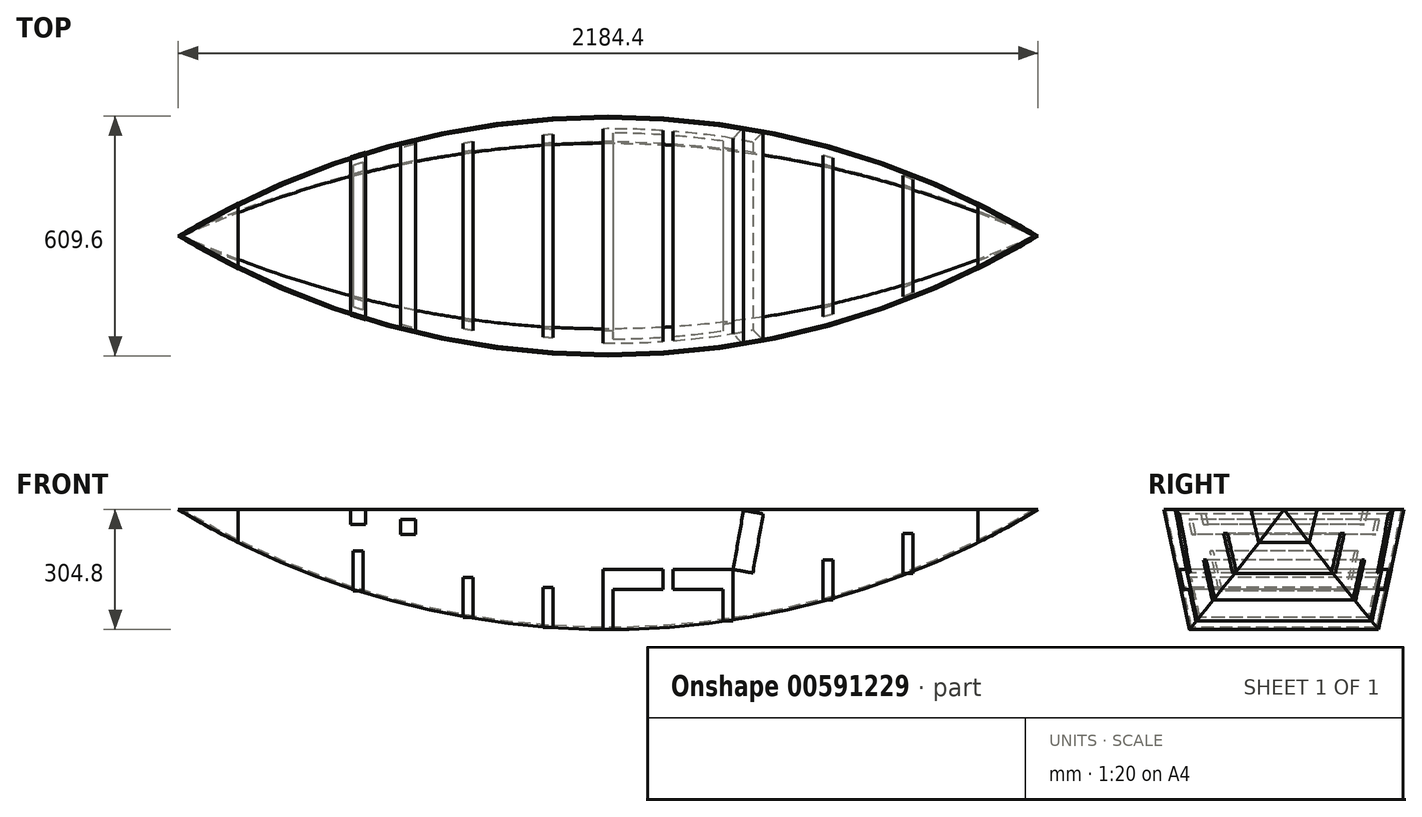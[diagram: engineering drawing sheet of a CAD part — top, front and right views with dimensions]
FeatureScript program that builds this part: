
annotation { "Feature Type Name" : "Feature", "Feature Type Description" : "" }
export const myFeature = defineFeature(function(context is Context, id is Id, definition is map)
    precondition{}
    {
        {
            var Q0;
            Q0=qCreatedBy(makeId("Front.planeOp"),FACE);
            var sketch = newSketch(context, id + "F0", { "sketchPlane" : qUnion([Q0])});
            skLineSegment(sketch, "E0", {"start": v(0, 0) * mm, "end": v(2184.4, 0) * mm});
            skArc(sketch, "E1", {"start": v(0, 0) * mm, "mid": v(1092.2, -304.8) * mm, "end": v(2184.4, 0) * mm});
            skSolve(sketch);
        }
        {
            var Q0;
            Q0 = qSketchRegion(id + "F0", true);
            extrude(context, id + "F1", {"entities" : qUnion([Q0]), "oppositeDirection" : true, "depth" : 609.6 * mm, "offsetDistance" : 25.4 * mm});
        }
        {
            var Q0;
            Q0=makeQuery(id+"F1.opExtrude","SWEPT_FACE",FACE,{"disambiguationData":[OSD([sQuery(id+"F0.wireOp",EDGE,"E0")])]});
            var sketch = newSketch(context, id + "F2", { "sketchPlane" : qUnion([Q0])});
            skLineSegment(sketch, "E2", {"start": v(0, 304.8) * mm, "end": v(2184.4, 304.8) * mm});
            skArc(sketch, "E3", {"start": v(0, 304.8) * mm, "mid": v(1092.2, 0) * mm, "end": v(2184.4, 304.8) * mm});
            skArc(sketch, "E4", {"start": v(2184.4, 304.8) * mm, "mid": v(1092.2, 609.6) * mm, "end": v(0, 304.8) * mm});
            skLineSegment(sketch, "E5.bottom", {"start": v(-93.83, 720.8) * mm, "end": v(2286.33, 720.8) * mm});
            skLineSegment(sketch, "E5.top", {"start": v(-93.83, -163.14) * mm, "end": v(2286.33, -163.14) * mm});
            skLineSegment(sketch, "E5.left", {"start": v(-93.83, 720.8) * mm, "end": v(-93.83, -163.14) * mm});
            skLineSegment(sketch, "E5.right", {"start": v(2286.33, 720.8) * mm, "end": v(2286.33, -163.14) * mm});
            skSolve(sketch);
        }
        {
            var Q0;
            Q0 = qSketchRegion(id + "F2", true);
            extrude(context, id + "F3", {"entities" : qUnion([Q0]), "operationType" : NewBodyOperationType.REMOVE, "oppositeDirection" : true, "depth" : 508 * mm, "offsetDistance" : 25.4 * mm, "hasDraft" : true, "draftAngle" : 12 * degree});
        }
        {
            var Q0;
            Q0=makeQuery(id+"F1.opExtrude","SWEPT_FACE",FACE,{"disambiguationData":[OSD([sQuery(id+"F0.wireOp",EDGE,"E0")])]});
            shell(context, id + "F4", {"entities" : qUnion([Q0]), "thickness" : 5.16 * mm});
        }
        {
            var Q0;
            Q0=qCreatedBy(makeId("Front.planeOp"),FACE);
            var sketch = newSketch(context, id + "F5", { "sketchPlane" : qUnion([Q0])});
            skLineSegment(sketch, "E6.bottom", {"start": v(1079.5, -304.8) * mm, "end": v(1104.9, -304.8) * mm});
            skLineSegment(sketch, "E6.top", {"start": v(1079.5, -203.2) * mm, "end": v(1104.9, -203.2) * mm});
            skLineSegment(sketch, "E6.left", {"start": v(1079.5, -304.8) * mm, "end": v(1079.5, -203.2) * mm});
            skLineSegment(sketch, "E6.right", {"start": v(1104.9, -304.8) * mm, "end": v(1104.9, -203.2) * mm});
            skPoint(sketch, "E7", {"position": v(1092.2, -304.8) * mm});
            skPoint(sketch, "E8", {"position": v(1092.2, 0) * mm});
            skPoint(sketch, "E8.positionSnap0", {"position": v(1092.2, -203.2) * mm});
            skPoint(sketch, "E9", {"position": v(939.8, 0) * mm});
            skPoint(sketch, "E10", {"position": v(457.2, 0) * mm});
            skPoint(sketch, "E11", {"position": v(1397, 0) * mm});
            skPoint(sketch, "E12", {"position": v(1651, 0) * mm});
            skPoint(sketch, "E13", {"position": v(1854.2, 0) * mm});
            skArc(sketch, "E14.0", {"start": v(0, 0) * mm, "mid": v(1092.2, -304.8) * mm, "end": v(2184.4, 0) * mm});
            skPoint(sketch, "E15", {"position": v(939.8, -299.29) * mm});
            skPoint(sketch, "E16", {"position": v(457.2, -206.95) * mm});
            skPoint(sketch, "E17", {"position": v(1397, -282.66) * mm});
            skPoint(sketch, "E18", {"position": v(1651, -229.43) * mm});
            skPoint(sketch, "E19", {"position": v(1854.2, -162.35) * mm});
            skLineSegment(sketch, "E20.bottom", {"start": v(927.1, -197.69) * mm, "end": v(952.5, -197.69) * mm});
            skLineSegment(sketch, "E20.top", {"start": v(927.1, -299.29) * mm, "end": v(952.5, -299.29) * mm});
            skLineSegment(sketch, "E20.left", {"start": v(927.1, -197.69) * mm, "end": v(927.1, -299.29) * mm});
            skLineSegment(sketch, "E20.right", {"start": v(952.5, -197.69) * mm, "end": v(952.5, -299.29) * mm});
            skLineSegment(sketch, "E21.bottom", {"start": v(444.5, -105.35) * mm, "end": v(469.9, -105.35) * mm});
            skLineSegment(sketch, "E21.top", {"start": v(444.5, -206.95) * mm, "end": v(469.9, -206.95) * mm});
            skLineSegment(sketch, "E21.left", {"start": v(444.5, -105.35) * mm, "end": v(444.5, -206.95) * mm});
            skLineSegment(sketch, "E21.right", {"start": v(469.9, -105.35) * mm, "end": v(469.9, -206.95) * mm});
            skLineSegment(sketch, "E22.bottom", {"start": v(1384.3, -203.2) * mm, "end": v(1409.7, -203.2) * mm});
            skLineSegment(sketch, "E22.top", {"start": v(1384.3, -282.66) * mm, "end": v(1409.7, -282.66) * mm});
            skLineSegment(sketch, "E22.left", {"start": v(1384.3, -203.2) * mm, "end": v(1384.3, -282.66) * mm});
            skLineSegment(sketch, "E22.right", {"start": v(1409.7, -203.2) * mm, "end": v(1409.7, -282.66) * mm});
            skLineSegment(sketch, "E23.bottom", {"start": v(1638.3, -127.83) * mm, "end": v(1663.7, -127.83) * mm});
            skLineSegment(sketch, "E23.top", {"start": v(1638.3, -229.43) * mm, "end": v(1663.7, -229.43) * mm});
            skLineSegment(sketch, "E23.left", {"start": v(1638.3, -127.83) * mm, "end": v(1638.3, -229.43) * mm});
            skLineSegment(sketch, "E23.right", {"start": v(1663.7, -127.83) * mm, "end": v(1663.7, -229.43) * mm});
            skLineSegment(sketch, "E24.bottom", {"start": v(1841.5, -60.75) * mm, "end": v(1866.9, -60.75) * mm});
            skLineSegment(sketch, "E24.top", {"start": v(1841.5, -162.35) * mm, "end": v(1866.9, -162.35) * mm});
            skLineSegment(sketch, "E24.left", {"start": v(1841.5, -60.75) * mm, "end": v(1841.5, -162.35) * mm});
            skLineSegment(sketch, "E24.right", {"start": v(1866.9, -60.75) * mm, "end": v(1866.9, -162.35) * mm});
            skPoint(sketch, "E25", {"position": v(1397, -203.2) * mm});
            skPoint(sketch, "E26", {"position": v(1244.6, 0) * mm});
            skLineSegment(sketch, "E27.bottom", {"start": v(1079.5, -152.4) * mm, "end": v(1231.9, -152.4) * mm});
            skLineSegment(sketch, "E27.top", {"start": v(1079.5, -203.2) * mm, "end": v(1231.9, -203.2) * mm});
            skLineSegment(sketch, "E27.left", {"start": v(1079.5, -152.4) * mm, "end": v(1079.5, -203.2) * mm});
            skLineSegment(sketch, "E27.right", {"start": v(1231.9, -152.4) * mm, "end": v(1231.9, -203.2) * mm});
            skLineSegment(sketch, "E28.bottom", {"start": v(1257.3, -152.4) * mm, "end": v(1409.7, -152.4) * mm});
            skLineSegment(sketch, "E28.top", {"start": v(1257.3, -203.2) * mm, "end": v(1409.7, -203.2) * mm});
            skLineSegment(sketch, "E28.left", {"start": v(1257.3, -152.4) * mm, "end": v(1257.3, -203.2) * mm});
            skLineSegment(sketch, "E28.right", {"start": v(1409.7, -152.4) * mm, "end": v(1409.7, -203.2) * mm});
            skLineSegment(sketch, "E29", {"start": v(1409.7, -152.4) * mm, "end": v(1436.16, -2.32) * mm});
            skLineSegment(sketch, "E30", {"start": v(1436.16, -2.32) * mm, "end": v(1486.2, -11.14) * mm});
            skLineSegment(sketch, "E31", {"start": v(1486.2, -11.14) * mm, "end": v(1459.73, -161.22) * mm});
            skLineSegment(sketch, "E32", {"start": v(1459.73, -161.22) * mm, "end": v(1409.7, -152.4) * mm});
            skLineSegment(sketch, "E33.bottom", {"start": v(438.16, 0) * mm, "end": v(476.26, 0) * mm});
            skLineSegment(sketch, "E33.top", {"start": v(438.16, -38.1) * mm, "end": v(476.26, -38.1) * mm});
            skLineSegment(sketch, "E33.left", {"start": v(438.16, 0) * mm, "end": v(438.16, -38.1) * mm});
            skLineSegment(sketch, "E33.right", {"start": v(476.26, 0) * mm, "end": v(476.26, -38.1) * mm});
            skPoint(sketch, "E34", {"position": v(736.6, 0) * mm});
            skPoint(sketch, "E35", {"position": v(736.6, -274.6) * mm});
            skLineSegment(sketch, "E36.bottom", {"start": v(749.3, -173) * mm, "end": v(723.9, -173) * mm});
            skLineSegment(sketch, "E36.top", {"start": v(749.3, -274.6) * mm, "end": v(723.9, -274.6) * mm});
            skLineSegment(sketch, "E36.left", {"start": v(749.3, -173) * mm, "end": v(749.3, -274.6) * mm});
            skLineSegment(sketch, "E36.right", {"start": v(723.9, -173) * mm, "end": v(723.9, -274.6) * mm});
            skPoint(sketch, "E37", {"position": v(584.2, 0) * mm});
            skLineSegment(sketch, "E38.bottom", {"start": v(565.15, -25.4) * mm, "end": v(603.25, -25.4) * mm});
            skLineSegment(sketch, "E38.top", {"start": v(565.15, -63.5) * mm, "end": v(603.25, -63.5) * mm});
            skLineSegment(sketch, "E38.left", {"start": v(565.15, -25.4) * mm, "end": v(565.15, -63.5) * mm});
            skLineSegment(sketch, "E38.right", {"start": v(603.25, -25.4) * mm, "end": v(603.25, -63.5) * mm});
            skPoint(sketch, "E39", {"position": v(584.2, -25.4) * mm});
            skLineSegment(sketch, "E40", {"start": v(0, 0) * mm, "end": v(152.4, 0) * mm});
            skLineSegment(sketch, "E41", {"start": v(152.4, 0) * mm, "end": v(152.4, -83.86) * mm});
            skLineSegment(sketch, "E42", {"start": v(2184.4, 0) * mm, "end": v(2032, 0) * mm});
            skLineSegment(sketch, "E43", {"start": v(2032, 0) * mm, "end": v(2032, -83.86) * mm});
            skSolve(sketch);
        }
        {
            var Q0;
            Q0 = qSketchRegion(id + "F5", true);
            extrude(context, id + "F6", {"entities" : qUnion([Q0]), "oppositeDirection" : true, "depth" : 762 * mm, "offsetDistance" : 25.4 * mm});
        }
        {
            var Q0;
            Q0=qCreatedBy(makeId("Top.planeOp"),FACE);
            var sketch = newSketch(context, id + "F7", { "sketchPlane" : qUnion([Q0])});
            skArc(sketch, "E44.0", {"start": v(2184.4, 304.8) * mm, "mid": v(1092.2, 609.6) * mm, "end": v(0, 304.8) * mm});
            skArc(sketch, "E45.0", {"start": v(0, 304.8) * mm, "mid": v(1092.2, 0) * mm, "end": v(2184.4, 304.8) * mm});
            skLineSegment(sketch, "E46.bottom", {"start": v(-50.49, 808.31) * mm, "end": v(2257.41, 808.31) * mm});
            skLineSegment(sketch, "E46.top", {"start": v(-50.49, -74.01) * mm, "end": v(2257.41, -74.01) * mm});
            skLineSegment(sketch, "E46.left", {"start": v(-50.49, 808.31) * mm, "end": v(-50.49, -74.01) * mm});
            skLineSegment(sketch, "E46.right", {"start": v(2257.41, 808.31) * mm, "end": v(2257.41, -74.01) * mm});
            skSolve(sketch);
        }
        {
            var Q0;
            Q0 = qSketchRegion(id + "F7", true);
            extrude(context, id + "F8", {"entities" : qUnion([Q0]), "operationType" : NewBodyOperationType.REMOVE, "oppositeDirection" : true, "depth" : 508 * mm, "offsetDistance" : 25.4 * mm, "hasDraft" : true, "draftAngle" : 12 * degree});
        }
    });
